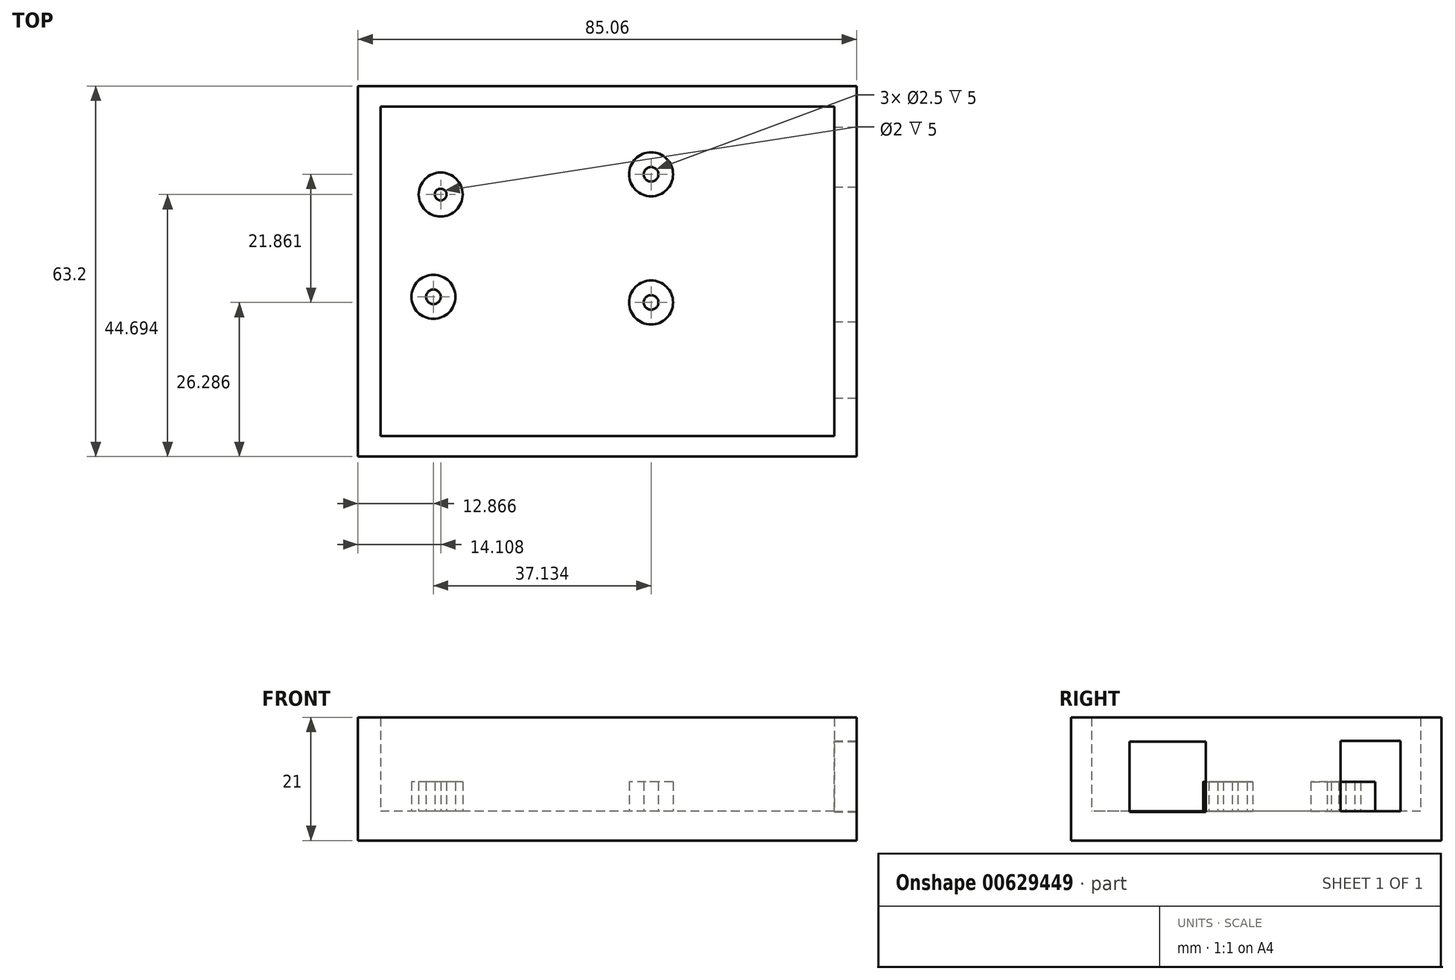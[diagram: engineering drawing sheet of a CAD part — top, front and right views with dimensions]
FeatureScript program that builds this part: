
annotation { "Feature Type Name" : "Feature", "Feature Type Description" : "" }
export const myFeature = defineFeature(function(context is Context, id is Id, definition is map)
    precondition{}
    {
        {
            var Q0;
            Q0=qCreatedBy(makeId("Top.planeOp"),FACE);
            var sketch = newSketch(context, id + "F0", { "sketchPlane" : qUnion([Q0])});
            skLineSegment(sketch, "E0.bottom", {"start": v(-42.53, 31.6) * mm, "end": v(42.53, 31.6) * mm});
            skLineSegment(sketch, "E0.top", {"start": v(-42.53, -31.6) * mm, "end": v(42.53, -31.6) * mm});
            skLineSegment(sketch, "E0.left", {"start": v(-42.53, 31.6) * mm, "end": v(-42.53, -31.6) * mm});
            skLineSegment(sketch, "E0.right", {"start": v(42.53, 31.6) * mm, "end": v(42.53, -31.6) * mm});
            skPoint(sketch, "E0.middle", {"position": v(0, 0) * mm});
            skSolve(sketch);
        }
        {
            var Q0;
            Q0=makeQuery(id+"F0.imprint","IMPRINT",FACE,{"disambiguationData":[TD([[makeQuery(id+"F0.imprint","IMPRINT",EDGE,{"derivedFrom":sQuery(id+"F0.wireOp",EDGE,"E0.bottom")}),-1.0]])]});
            extrude(context, id + "F1", {"entities" : qUnion([Q0]), "depth" : 5 * mm, "offsetDistance" : 25 * mm});
        }
        {
            var Q0;
            Q0=makeQuery(id+"F1.opExtrude","CAP_FACE",FACE,{"disambiguationData":[OSD([sQuery(id+"F0.wireOp",EDGE,"E0.bottom"),sQuery(id+"F0.wireOp",EDGE,"E0.top"),sQuery(id+"F0.wireOp",EDGE,"E0.left"),sQuery(id+"F0.wireOp",EDGE,"E0.right")])],"isStart":false});
            var sketch = newSketch(context, id + "F2", { "sketchPlane" : qUnion([Q0])});
            skLineSegment(sketch, "E1.bottom", {"start": v(42.53, 31.6) * mm, "end": v(-42.53, 31.6) * mm});
            skLineSegment(sketch, "E1.top", {"start": v(42.53, -31.6) * mm, "end": v(-42.53, -31.6) * mm});
            skLineSegment(sketch, "E1.left", {"start": v(42.53, 31.6) * mm, "end": v(42.53, -31.6) * mm});
            skLineSegment(sketch, "E1.right", {"start": v(-42.53, 31.6) * mm, "end": v(-42.53, -31.6) * mm});
            skPoint(sketch, "E1.middle", {"position": v(0, 0) * mm});
            skLineSegment(sketch, "E2.bottom", {"start": v(38.7, 28.07) * mm, "end": v(-38.7, 28.07) * mm});
            skLineSegment(sketch, "E2.top", {"start": v(38.7, -28.07) * mm, "end": v(-38.7, -28.07) * mm});
            skLineSegment(sketch, "E2.left", {"start": v(38.7, 28.07) * mm, "end": v(38.7, -28.07) * mm});
            skLineSegment(sketch, "E2.right", {"start": v(-38.7, 28.07) * mm, "end": v(-38.7, -28.07) * mm});
            skSolve(sketch);
        }
        {
            var Q0;
            Q0 = qSketchRegion(id + "F2", true);
            extrude(context, id + "F3", {"entities" : qUnion([Q0]), "operationType" : NewBodyOperationType.ADD, "depth" : 16 * mm, "offsetDistance" : 25 * mm});
        }
        {
            var Q0;
            Q0=makeQuery(id+"F3.boolean.opBoolean","MERGE",FACE,{"derivedFrom":[makeQuery(id+"F1.opExtrude","SWEPT_FACE",FACE,{"disambiguationData":[OSD([sQuery(id+"F0.wireOp",EDGE,"E0.right")])]}),makeQuery(id+"F3.opExtrude","SWEPT_FACE",FACE,{"disambiguationData":[OSD([sQuery(id+"F2.wireOp",EDGE,"E1.left")])]})]});
            var sketch = newSketch(context, id + "F4", { "sketchPlane" : qUnion([Q0])});
            skLineSegment(sketch, "E3.bottom", {"start": v(24.6, 5) * mm, "end": v(14.4, 5) * mm});
            skLineSegment(sketch, "E3.top", {"start": v(24.6, 17) * mm, "end": v(14.4, 17) * mm});
            skLineSegment(sketch, "E3.left", {"start": v(24.6, 5) * mm, "end": v(24.6, 17) * mm});
            skLineSegment(sketch, "E3.right", {"start": v(14.4, 5) * mm, "end": v(14.4, 17) * mm});
            skPoint(sketch, "E3.middle", {"position": v(19.5, 11) * mm});
            skSolve(sketch);
        }
        {
            var Q0;
            Q0 = qSketchRegion(id + "F4", true);
            extrude(context, id + "F5", {"entities" : qUnion([Q0]), "operationType" : NewBodyOperationType.REMOVE, "oppositeDirection" : true, "depth" : 25 * mm, "offsetDistance" : 25 * mm});
        }
        {
            var Q0;
            Q0=makeQuery(id+"F3.boolean.opBoolean","MERGE",FACE,{"derivedFrom":[makeQuery(id+"F1.opExtrude","SWEPT_FACE",FACE,{"disambiguationData":[OSD([sQuery(id+"F0.wireOp",EDGE,"E0.right")])]}),makeQuery(id+"F3.opExtrude","SWEPT_FACE",FACE,{"disambiguationData":[OSD([sQuery(id+"F2.wireOp",EDGE,"E1.left")])]})]});
            var sketch = newSketch(context, id + "F6", { "sketchPlane" : qUnion([Q0])});
            skLineSegment(sketch, "E4.bottom", {"start": v(-21.6, 16.86) * mm, "end": v(-8.6, 16.86) * mm});
            skLineSegment(sketch, "E4.top", {"start": v(-21.6, 4.86) * mm, "end": v(-8.6, 4.86) * mm});
            skLineSegment(sketch, "E4.left", {"start": v(-21.6, 16.86) * mm, "end": v(-21.6, 4.86) * mm});
            skLineSegment(sketch, "E4.right", {"start": v(-8.6, 16.86) * mm, "end": v(-8.6, 4.86) * mm});
            skPoint(sketch, "E4.middle", {"position": v(-15.1, 10.86) * mm});
            skSolve(sketch);
        }
        {
            var Q0;
            Q0 = qSketchRegion(id + "F6", true);
            var Q1;
            Q1=makeQuery(id+"F3.opExtrude","SWEPT_FACE",FACE,{"disambiguationData":[OSD([sQuery(id+"F2.wireOp",EDGE,"E2.left")])]});
            extrude(context, id + "F7", {"entities" : qUnion([Q0]), "operationType" : NewBodyOperationType.REMOVE, "endBound" : BoundingType.UP_TO_SURFACE, "oppositeDirection" : true, "depth" : 25 * mm, "endBoundEntityFace" : qUnion([Q1]), "offsetDistance" : 25 * mm});
        }
        {
            var Q0;
            Q0=makeQuery(id+"F2.imprint","IMPRINT",FACE,{"disambiguationData":[TD([[makeQuery(id+"F2.imprint","IMPRINT",EDGE,{"derivedFrom":sQuery(id+"F2.wireOp",EDGE,"E2.bottom")}),1.0]])]});
            var sketch = newSketch(context, id + "F8", { "sketchPlane" : qUnion([Q0])});
            skCircle(sketch, "E5", {"center": v(-28.42, 13.1) * mm, "radius": 3.75 * mm});
            skCircle(sketch, "E6", {"center": v(-28.42, 13.1) * mm, "radius": 1 * mm});
            skCircle(sketch, "E7", {"center": v(-29.66, -4.35) * mm, "radius": 3.75 * mm});
            skCircle(sketch, "E8", {"center": v(-29.66, -4.35) * mm, "radius": 1.25 * mm});
            skCircle(sketch, "E9", {"center": v(7.47, 16.55) * mm, "radius": 3.75 * mm});
            skCircle(sketch, "E10", {"center": v(7.47, 16.55) * mm, "radius": 1.25 * mm});
            skCircle(sketch, "E11", {"center": v(7.47, -5.31) * mm, "radius": 3.75 * mm});
            skCircle(sketch, "E12", {"center": v(7.47, -5.31) * mm, "radius": 1.25 * mm});
            skSolve(sketch);
        }
        {
            var Q0;
            Q0 = qSketchRegion(id + "F8", true);
            extrude(context, id + "F9", {"entities" : qUnion([Q0]), "operationType" : NewBodyOperationType.ADD, "depth" : 5 * mm, "offsetDistance" : 25 * mm});
        }
    });
